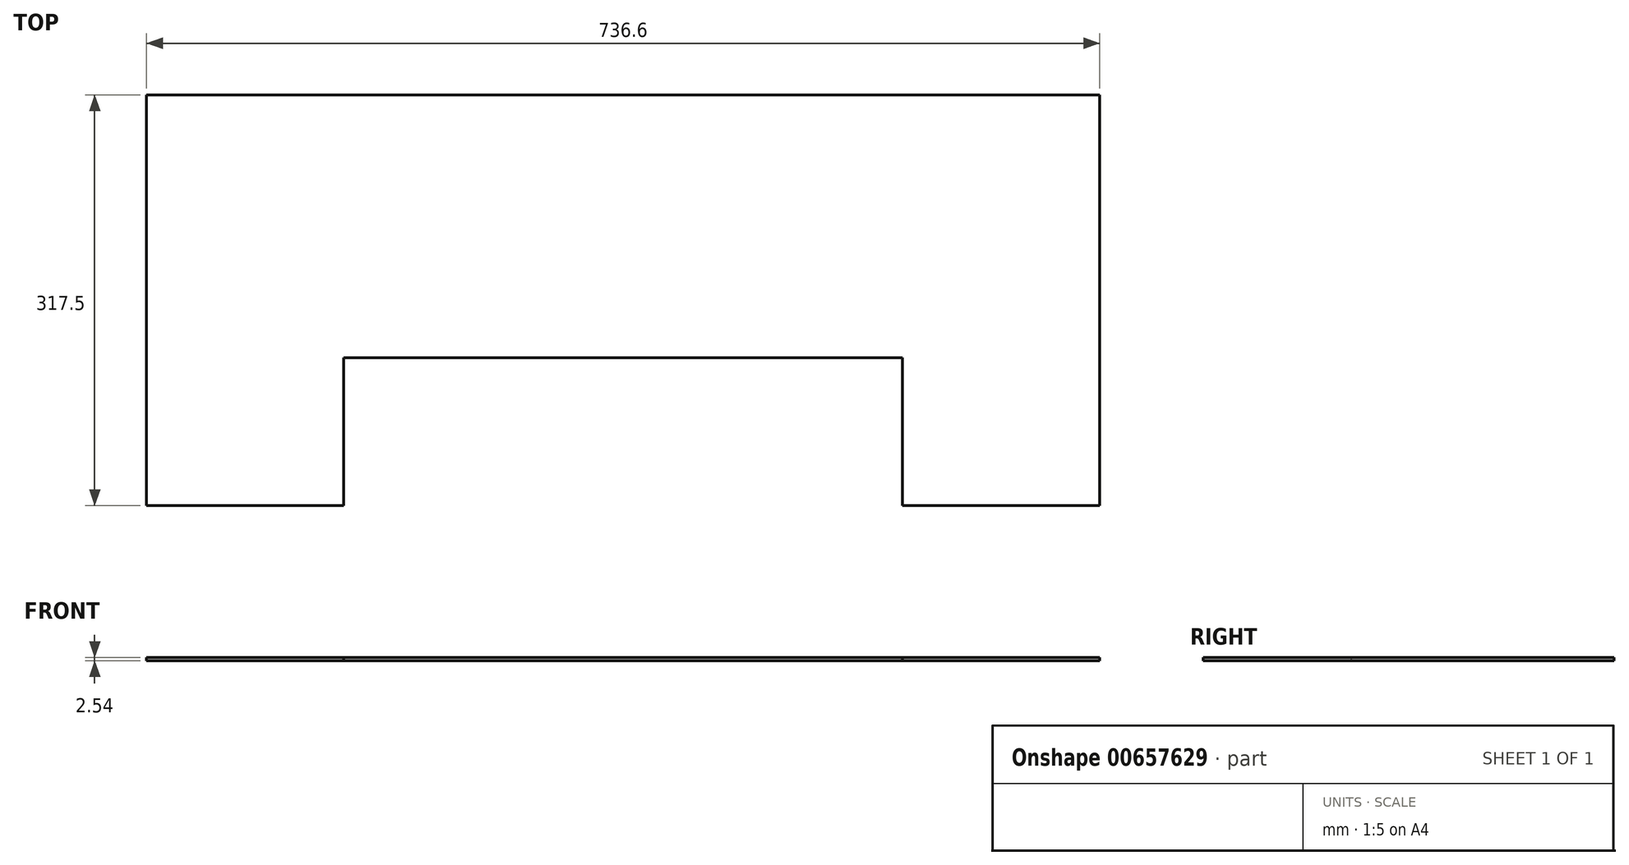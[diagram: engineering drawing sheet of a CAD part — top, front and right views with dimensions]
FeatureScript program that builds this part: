
annotation { "Feature Type Name" : "Feature", "Feature Type Description" : "" }
export const myFeature = defineFeature(function(context is Context, id is Id, definition is map)
    precondition{}
    {
        {
            var Q0;
            Q0=qCreatedBy(makeId("Top.planeOp"),FACE);
            var sketch = newSketch(context, id + "F0", { "sketchPlane" : qUnion([Q0])});
            skLineSegment(sketch, "E0.bottom", {"start": v(0, 0) * mm, "end": v(736.6, 0) * mm});
            skLineSegment(sketch, "E0.top", {"start": v(0, -317.5) * mm, "end": v(736.6, -317.5) * mm});
            skLineSegment(sketch, "E0.left", {"start": v(0, 0) * mm, "end": v(0, -317.5) * mm});
            skLineSegment(sketch, "E0.right", {"start": v(736.6, 0) * mm, "end": v(736.6, -317.5) * mm});
            skLineSegment(sketch, "E1.bottom", {"start": v(152.4, -317.5) * mm, "end": v(584.2, -317.5) * mm});
            skLineSegment(sketch, "E1.top", {"start": v(152.4, -203.2) * mm, "end": v(584.2, -203.2) * mm});
            skLineSegment(sketch, "E1.left", {"start": v(152.4, -317.5) * mm, "end": v(152.4, -203.2) * mm});
            skLineSegment(sketch, "E1.right", {"start": v(584.2, -317.5) * mm, "end": v(584.2, -203.2) * mm});
            skSolve(sketch);
        }
        {
            var Q0;
            Q0=makeQuery(id+"F0.imprint","IMPRINT",FACE,{"disambiguationData":[TD([[makeQuery(id+"F0.imprint","IMPRINT",EDGE,{"derivedFrom":sQuery(id+"F0.wireOp",EDGE,"E0.bottom")}),-1.0]])]});
            extrude(context, id + "F1", {"entities" : qUnion([Q0]), "depth" : 2.54 * mm, "offsetDistance" : 25.4 * mm});
        }
    });
